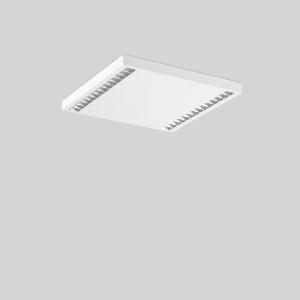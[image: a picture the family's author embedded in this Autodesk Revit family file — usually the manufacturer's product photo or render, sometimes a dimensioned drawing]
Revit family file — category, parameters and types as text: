
# Revit family: sonis_901689_002_1_76_de78
name_source: partatom
category: Lighting Fixtures
units: mm (PartAtom-declared; Revit-internal decimal feet)

## family parameters
Cut with Voids When Loaded = No
Host = Face
Light Source = No
Part Type = Normal
Room Calculation Point = No
Round Connector Dimension = Use Diameter
Shared = No

## types (1)
- SONIS (1 x LED Modul 840, 3450 lm, 4000)
    Apparent Load = 26 VA
    CIE Flux Codes = 83 100 100 100 100
    Color Rendering = 80
    Color Temperature = 4000
    Default Elevation = 1800 mm
    Description = Series: SONIS
High-efficiency LED louvre surface-mounted luminaire. Housing: metal, powder-coated. Alea optical system: Reflector structure (ABS, Aluminium-coated, highly polished) with integrated diffuser made of non-yellowing plastic (PMMA) opal for glare-free light at the workstation. Narrow beam, brilliant luminous effect. Suitable for Ceiling mounting. Driver integrated. Perfect for office areas (RUG < 19) and environments with computer screens in accordance with EN 12464-1. 
Colour: white
Length: 602 mm
Width: 602 mm
Height: 47 mm
Lamp: LED
Socket: without socket
Colour temperature: 4000K
Colour rendering index (CRI): 80
System power: 26 W
Rated luminous flux: 3450 lm
Luminous efficiency: 133 lm/W
Control gear: Converter, dimmable, DALI
Protection class: I
Type of protection: IP 20
    Height = 47 mm
    Lamp = 1 x LED Modul 840
    Lamp Light Flux = 3450 lm
    Lamp count = 1
    Length = 602 mm
    Lifetime = 50000 h
    Luminous efficacy = 133 lm/W
    Manufacturer = RZB
    ModVariant = No
    Model = 901689.002.1.76
    Mounting Place = Ceiling
    Mounting Type = Surface mounted
    Number of Poles = 1
    OnlyDefault = Yes
    Power Factor = 1
    Product Name = SONIS
    Product group = Surface mounted modular luminaires
    ProductGroupID = 306
    Protection Class = Protection class I
    Protection Degree = IP 20
    RLX_Detail_Level = 1
    RLX_Emergency_Light_Flux = 0 lm
    RLX_Emergency_Type = 0
    RLX_Emergency_Type_DB = No
    RlxData = <blob elided: 20989 chars, md5=f50ea439>
    Socket = socket
    Standby Power = 0 W
    System Light Flux = 3450 lm
    System Power = 26 W
    Type Comments = Product without accessories
    Type Image = 901625.002.jpg
    URL = http://relux.com
    VarID = ---
    Voltage = 230 V
    Voltage Range = 220-240 V
    Weight = 0.00 kg
    Width = 602 mm

## geometry (parser evidence)
native form markers: Blend x4, Sweep x13
no freeform markers — native parametric forms only
